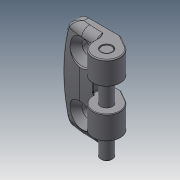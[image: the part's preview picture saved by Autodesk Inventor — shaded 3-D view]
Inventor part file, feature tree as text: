
AUTODESK INVENTOR PART (.ipt)
format: ipt  version: 2018.3 (Build 223284000, 284)  size: 441,856 bytes
history: native  units: in
note: dims shown in document units (in); Inventor stores cm internally (conversion verified against a paired STEP export)
features: mirror x2, revolve x1
ambient origin geometry x8: Origin, YZ Plane, XZ Plane, XY Plane, X Axis, Y Axis, Z Axis, Center Point
bodies: Solid1 (feature_tree), Solid2 (feature_tree), Solid3 (feature_tree)
feature tree (3):
  revolve  "Revolve1"  [1 undecoded]
  mirror  "Mirror3"
  mirror  "Mirror1"
note: 1 required parameter value undecoded (feature->parameter linkage not recoverable at this tier; creation-order binding heuristic only, values carry confidence <= 0.55)
